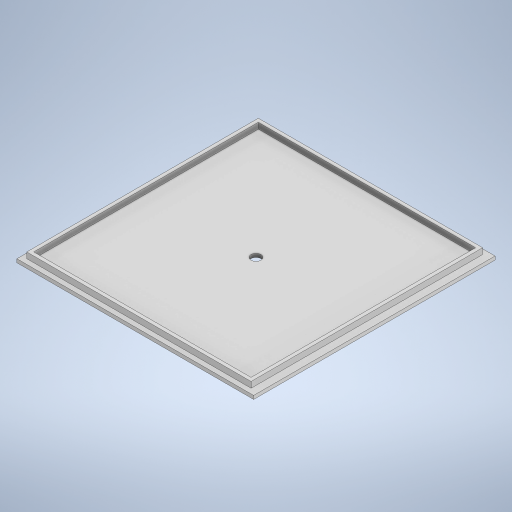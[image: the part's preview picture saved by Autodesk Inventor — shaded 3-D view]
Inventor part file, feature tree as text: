
AUTODESK INVENTOR PART (.ipt)
format: ipt  version: 2024 (Build 280153000, 153)  size: 564,736 bytes
history: native  units: mm
features: extrude x3, sketch x2
ambient origin geometry x8: Origin, YZ Plane, XZ Plane, XY Plane, X Axis, Y Axis, Z Axis, Center Point
bodies: Solid1 (feature_tree)
feature tree (5):
  sketch  "Sketch1"  dims[d0=101.0mm d1=103.0mm]
  extrude  "Extrusion1"  Depth=103.0mm
  extrude  "Extrusion2"  Depth=3.2mm
  extrude  "Extrusion3"  Depth=1.5mm
  sketch  "Sketch2"  dims[d2=2.1mm d3=3.2mm d4=1.5mm d5=1.5mm d6=0.0mm d7=4.0mm d8=0.0mm d9=4.2mm d10=4.0mm d11=0.0mm]
